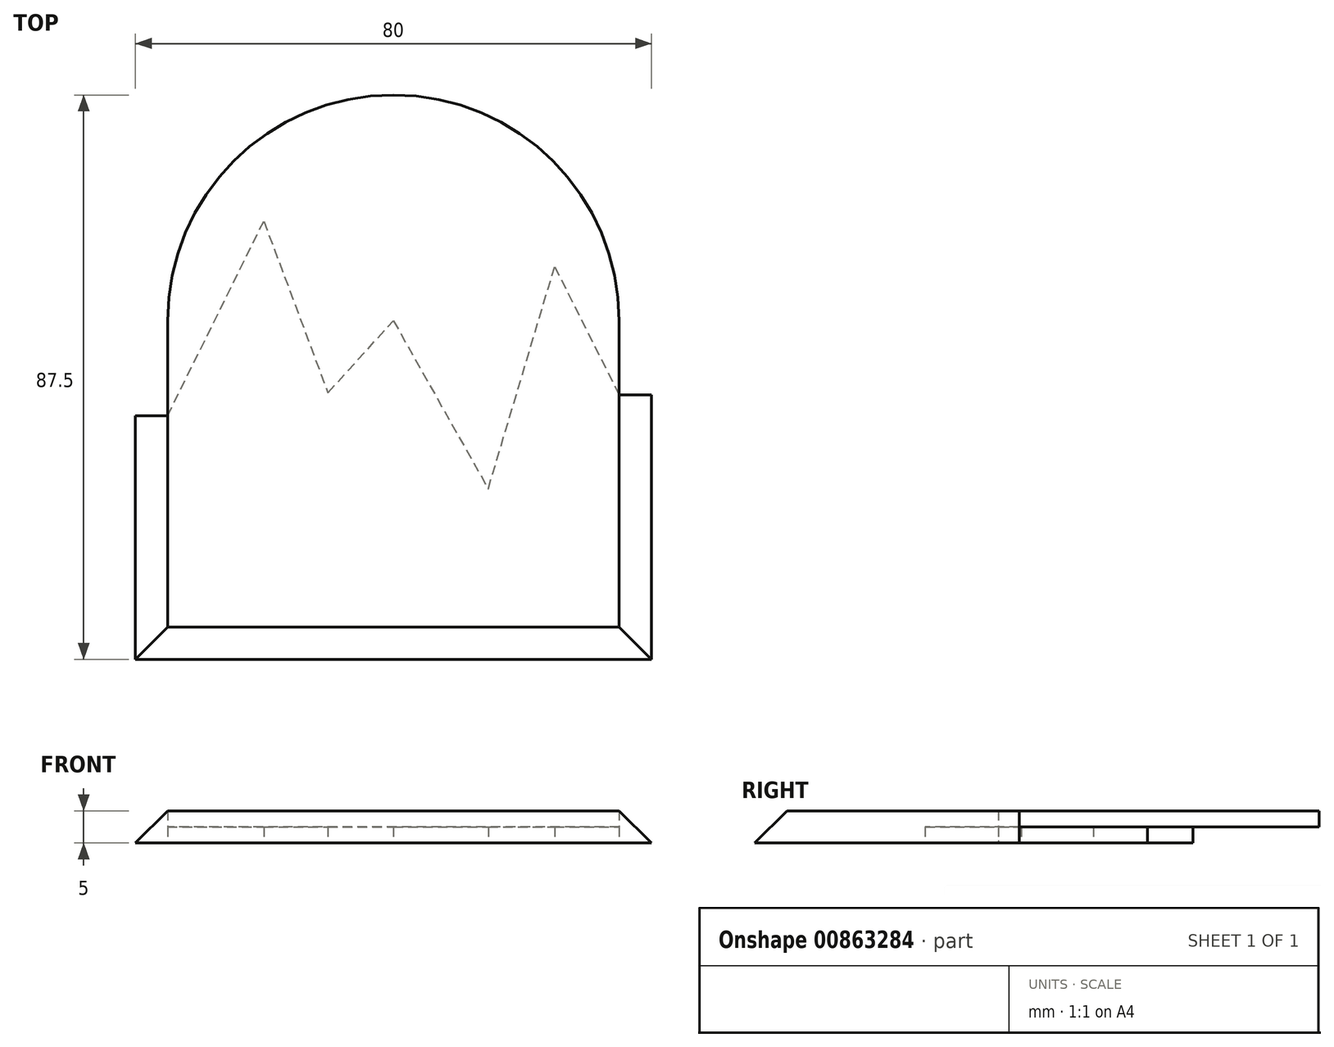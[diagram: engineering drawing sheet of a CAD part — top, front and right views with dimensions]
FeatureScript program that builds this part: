
annotation { "Feature Type Name" : "Feature", "Feature Type Description" : "" }
export const myFeature = defineFeature(function(context is Context, id is Id, definition is map)
    precondition{}
    {
        {
            var Q0;
            Q0=qCreatedBy(makeId("Top.planeOp"),FACE);
            var sketch = newSketch(context, id + "F0", { "sketchPlane" : qUnion([Q0])});
            skLineSegment(sketch, "E0.bottom", {"start": v(35, -47.5) * mm, "end": v(-35, -47.5) * mm});
            skLineSegment(sketch, "E0.top", {"start": v(35, 47.5) * mm, "end": v(-35, 47.5) * mm});
            skLineSegment(sketch, "E0.left", {"start": v(35, -47.5) * mm, "end": v(35, 47.5) * mm});
            skLineSegment(sketch, "E0.right", {"start": v(-35, -47.5) * mm, "end": v(-35, 47.5) * mm});
            skLineSegment(sketch, "E1.bottom", {"start": v(40, -52.5) * mm, "end": v(-40, -52.5) * mm});
            skLineSegment(sketch, "E1.top", {"start": v(40, 52.5) * mm, "end": v(-40, 52.5) * mm});
            skLineSegment(sketch, "E1.left", {"start": v(40, -52.5) * mm, "end": v(40, 52.5) * mm});
            skLineSegment(sketch, "E1.right", {"start": v(-40, -52.5) * mm, "end": v(-40, 52.5) * mm});
            skLineSegment(sketch, "E2", {"start": v(-35, -14.74) * mm, "end": v(-20.1, 15.44) * mm});
            skLineSegment(sketch, "E3", {"start": v(-20.1, 15.44) * mm, "end": v(-10.15, -11.19) * mm});
            skLineSegment(sketch, "E4", {"start": v(-10.15, -11.19) * mm, "end": v(0, 0) * mm});
            skLineSegment(sketch, "E5", {"start": v(0, 0) * mm, "end": v(14.7, -26.06) * mm});
            skLineSegment(sketch, "E6", {"start": v(14.7, -26.06) * mm, "end": v(25, 8.38) * mm});
            skLineSegment(sketch, "E7", {"start": v(25, 8.38) * mm, "end": v(35, -11.5) * mm});
            skLineSegment(sketch, "E8", {"start": v(35, -11.5) * mm, "end": v(40, -11.5) * mm});
            skLineSegment(sketch, "E9", {"start": v(-35, -14.74) * mm, "end": v(-40, -14.74) * mm});
            skSolve(sketch);
        }
        {
            var Q0;
            {var subQ1=sQuery(id+"F0.wireOp",EDGE,"E0.bottom");Q0=makeQuery(id+"F0.imprint","IMPRINT",FACE,{"disambiguationData":[TD([[makeQuery(id+"F0.imprint","IMPRINT",EDGE,{"derivedFrom":subQ1}),-1.0]])]});}
            var Q1;
            {var subQ2=sQuery(id+"F0.wireOp",EDGE,"E0.bottom");Q1=makeQuery(id+"F0.imprint","IMPRINT",FACE,{"disambiguationData":[TD([[makeQuery(id+"F0.imprint","IMPRINT",EDGE,{"derivedFrom":subQ2}),1.0]])]});}
            extrude(context, id + "F1", {"entities" : qUnion([Q0, Q1]), "depth" : 5 * mm, "offsetDistance" : 25 * mm});
        }
        {
            var Q0;
            Q0=makeQuery(id+"F1.opExtrude","CAP_EDGE",EDGE,{"disambiguationData":[OSD([sQuery(id+"F0.wireOp",EDGE,"E1.right")])],"isStart":false});
            var Q1;
            Q1=makeQuery(id+"F1.opExtrude","CAP_EDGE",EDGE,{"disambiguationData":[OSD([sQuery(id+"F0.wireOp",EDGE,"E1.bottom")])],"isStart":false});
            var Q2;
            Q2=makeQuery(id+"F1.opExtrude","CAP_EDGE",EDGE,{"disambiguationData":[OSD([sQuery(id+"F0.wireOp",EDGE,"E1.left")])],"isStart":false});
            chamfer(context, id + "F2", {"entities" : qUnion([Q0, Q1, Q2]), "width" : 5 * mm, "tangentPropagation" : true});
        }
        {
            var Q0;
            Q0=makeQuery(id+"F1.opExtrude","CAP_FACE",FACE,{"disambiguationData":[OSD([sQuery(id+"F0.wireOp",EDGE,"E1.bottom"),sQuery(id+"F0.wireOp",EDGE,"E1.left"),sQuery(id+"F0.wireOp",EDGE,"E1.right"),sQuery(id+"F0.wireOp",EDGE,"E2"),sQuery(id+"F0.wireOp",EDGE,"E3"),sQuery(id+"F0.wireOp",EDGE,"E4"),sQuery(id+"F0.wireOp",EDGE,"E5"),sQuery(id+"F0.wireOp",EDGE,"E6"),sQuery(id+"F0.wireOp",EDGE,"E7"),sQuery(id+"F0.wireOp",EDGE,"E8"),sQuery(id+"F0.wireOp",EDGE,"E9")])],"isStart":false});
            var sketch = newSketch(context, id + "F3", { "sketchPlane" : qUnion([Q0])});
            skCircle(sketch, "E10", {"center": v(0, 0) * mm, "radius": 35 * mm});
            skLineSegment(sketch, "E11", {"start": v(35, -11.5) * mm, "end": v(35, 0) * mm});
            skLineSegment(sketch, "E12", {"start": v(-35, -14.74) * mm, "end": v(-35, 0) * mm});
            skLineSegment(sketch, "E13", {"start": v(-35, -14.74) * mm, "end": v(35, -14.74) * mm});
            skSolve(sketch);
        }
        {
            var Q0;
            {var subQ0=sQuery(id+"F3.wireOp",EDGE,"E13");var subQ1=makeQuery(id+"F1.opExtrude","CAP_EDGE",EDGE,{"disambiguationData":[OSD([sQuery(id+"F0.wireOp",EDGE,"E5")])],"isStart":false});var subQ2=makeQuery(id+"F3.imprint","INTERSECT",VERTEX,{"derivedFrom":[subQ1,subQ0]});Q0=makeQuery(id+"F3.imprint","IMPRINT",FACE,{"disambiguationData":[TD([[makeQuery(id+"F3.imprint","IMPRINT",EDGE,{"disambiguationData":[TD([[subQ2,-1.0]])],"derivedFrom":subQ0}),-1.0]])]});}
            var Q1;
            {var subQ13=makeQuery(id+"F1.opExtrude","CAP_EDGE",EDGE,{"disambiguationData":[OSD([sQuery(id+"F0.wireOp",EDGE,"E3")])],"isStart":false});Q1=makeQuery(id+"F3.imprint","IMPRINT",FACE,{"disambiguationData":[TD([[makeQuery(id+"F3.imprint","IMPRINT",EDGE,{"derivedFrom":subQ13}),1.0]])]});}
            var Q2;
            {var subQ0=sQuery(id+"F3.wireOp",EDGE,"E11");Q2=makeQuery(id+"F3.imprint","IMPRINT",FACE,{"disambiguationData":[TD([[makeQuery(id+"F3.imprint","IMPRINT",EDGE,{"derivedFrom":subQ0}),1.0]])]});}
            var Q3;
            {var subQ0=sQuery(id+"F3.wireOp",EDGE,"E12");Q3=makeQuery(id+"F3.imprint","IMPRINT",FACE,{"disambiguationData":[TD([[makeQuery(id+"F3.imprint","IMPRINT",EDGE,{"derivedFrom":subQ0}),-1.0]])]});}
            extrude(context, id + "F4", {"entities" : qUnion([Q0, Q1, Q2, Q3]), "operationType" : NewBodyOperationType.ADD, "oppositeDirection" : true, "depth" : 2.5 * mm, "offsetDistance" : 25 * mm});
        }
    });
